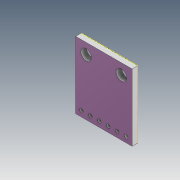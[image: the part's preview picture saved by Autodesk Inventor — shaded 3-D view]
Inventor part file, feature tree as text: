
AUTODESK INVENTOR PART (.ipt)
format: ipt  version: 2020 (Build 240168000, 168)  size: 336,384 bytes
history: native  units: in
note: dims shown in document units (in); Inventor stores cm internally (conversion verified against a paired STEP export)
features: sketch x3, extrude x2, chamfer x1, other x1
ambient origin geometry x8: Origin, YZ Plane, XZ Plane, XY Plane, X Axis, Y Axis, Z Axis, Center Point
bodies: Solid1 (feature_tree)
feature tree (7):
  extrude  "Extrusion1"  Depth=0.748in
  extrude  "Extrusion2"  Depth=0.0394in
  chamfer  "Chamfer1"  Distance=0.1181in
  sketch  "Sketch3"  dims[d5=0.1181in d6=0.1181in d7=0.063in d8=2.3622in d10=0.1in d11=0.3937in d13=0.3937in d15=0.063in d16=0.0in d17=0.2008in d18=0.1496in d19=0.4134in d20=0.0591in d21=0.0in d22=0.0118in d23=0.0787in d24=45.0deg]
  sketch  "Sketch1"  dims[d0=0.6299in d1=0.748in]
  sketch  "Sketch2"  dims[d3=0.1181in d4=0.0394in]
  other  "Image1"
